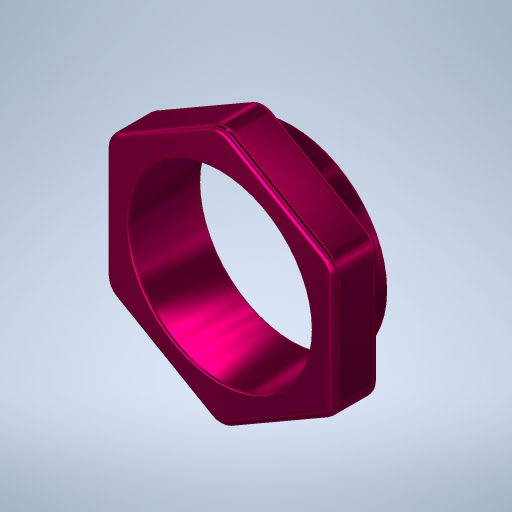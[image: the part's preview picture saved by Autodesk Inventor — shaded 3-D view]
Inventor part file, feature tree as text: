
AUTODESK INVENTOR PART (.ipt)
format: ipt  version: 2023.1 (Build 271208000, 208)  size: 368,640 bytes
history: native  units: in
note: dims shown in document units (in); Inventor stores cm internally (conversion verified against a paired STEP export)
features: extrude x3, fillet x3, sketch x3
ambient origin geometry x8: Origin, YZ Plane, XZ Plane, XY Plane, X Axis, Y Axis, Z Axis, Center Point
bodies: Solid1 (feature_tree)
feature tree (9):
  extrude  "Extrusion1"  Depth=0.075in TaperAngle=0.0deg
  extrude  "Extrusion2"  Depth=0.125in TaperAngle=0.0deg
  extrude  "Extrusion3"  Depth=0.125in TaperAngle=0.0deg
  fillet  "Fillet1"  Radius=0.05in
  fillet  "Fillet2"  Radius=0.015in
  fillet  "Fillet3"  Radius=0.005in
  sketch  "Sketch1"  dims[d0=0.525in d1=0.075in d2=0.0in]
  sketch  "Sketch2"  dims[d3=0.625in d4=0.125in d5=0.0in]
  sketch  "Sketch3"  dims[d6=0.5in d7=0.125in d8=0.0in d9=0.05in d10=0.015in d11=0.005in]
